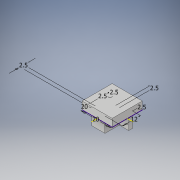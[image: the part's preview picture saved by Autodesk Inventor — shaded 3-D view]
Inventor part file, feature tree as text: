
AUTODESK INVENTOR PART (.ipt)
format: ipt  version: 2019 (Build 230136000, 136)  size: 115,200 bytes
history: native  units: mm
features: extrude x2, sketch x1
ambient origin geometry x8: Origin, YZ Plane, XZ Plane, XY Plane, X Axis, Y Axis, Z Axis, Center Point
bodies: Solid1 (feature_tree)
feature tree (3):
  sketch  "Sketch1"  dims[d0=20.0mm d1=20.0mm d2=2.5mm d3=2.5mm d4=12.0mm d5=2.5mm d6=2.5mm d7=2.5mm d8=10.0mm d9=0.0mm d10=5.0mm d11=0.0mm]
  extrude  "Extrusion1"  Depth=20.0mm
  extrude  "Extrusion2"  Depth=2.5mm
